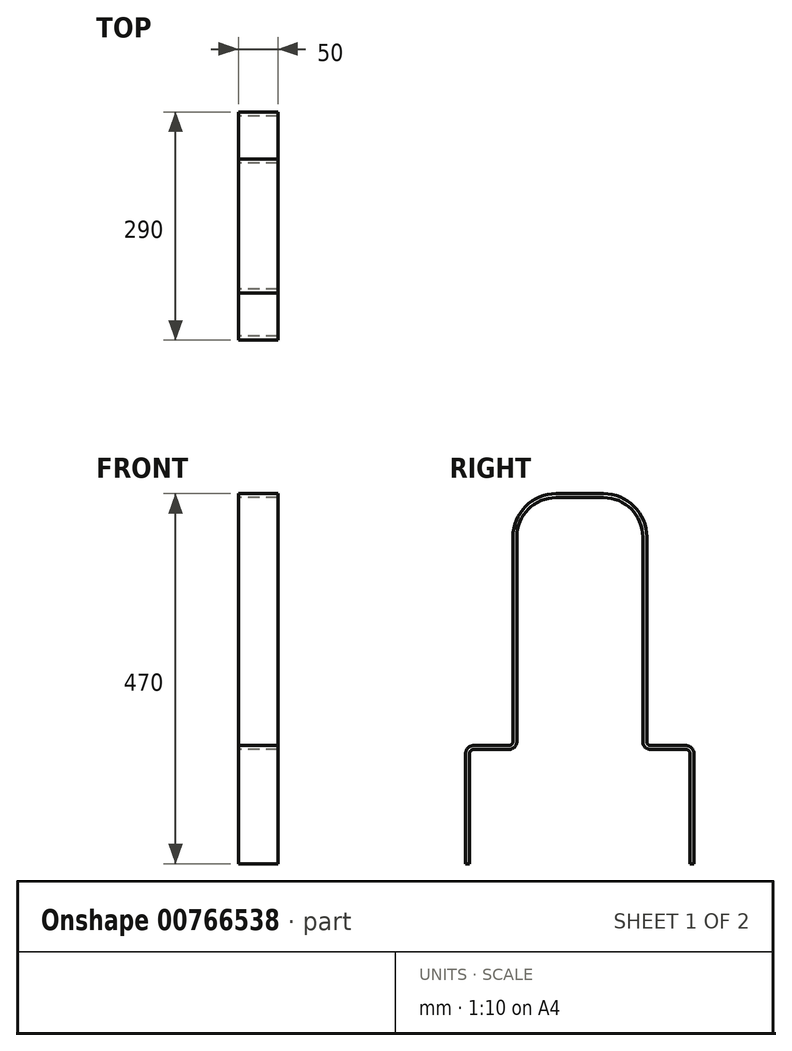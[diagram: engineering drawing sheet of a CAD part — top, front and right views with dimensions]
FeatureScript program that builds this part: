
annotation { "Feature Type Name" : "Feature", "Feature Type Description" : "" }
export const myFeature = defineFeature(function(context is Context, id is Id, definition is map)
    precondition{}
    {
        {
            var Q0;
            Q0=qCreatedBy(makeId("Right.planeOp"),FACE);
            var sketch = newSketch(context, id + "F0", { "sketchPlane" : qUnion([Q0])});
            skLineSegment(sketch, "E0", {"start": v(-145, 0) * mm, "end": v(-145, 140) * mm});
            skLineSegment(sketch, "E1", {"start": v(-135, 150) * mm, "end": v(-90, 150) * mm});
            skLineSegment(sketch, "E2", {"start": v(-85, 155) * mm, "end": v(-85, 415) * mm});
            skLineSegment(sketch, "E3", {"start": v(-30, 470) * mm, "end": v(0, 470) * mm});
            skLineSegment(sketch, "E4", {"start": v(-140, 0) * mm, "end": v(-140, 140) * mm});
            skLineSegment(sketch, "E5", {"start": v(-135, 145) * mm, "end": v(-90, 145) * mm});
            skLineSegment(sketch, "E6", {"start": v(-80, 155) * mm, "end": v(-80, 415) * mm});
            skLineSegment(sketch, "E7", {"start": v(-30, 465) * mm, "end": v(0, 465) * mm});
            skLineSegment(sketch, "E8", {"start": v(-140, 0) * mm, "end": v(-145, 0) * mm});
            skPoint(sketch, "E9.visualSharp", {"position": v(-165, 465) * mm});
            skLineSegment(sketch, "E9.filletArc", {"start": v(-80, 465) * mm, "end": v(-80, 465) * mm});
            skPoint(sketch, "E10.visualSharp", {"position": v(-85, 470) * mm});
            skArc(sketch, "E10.filletArc", {"start": v(-30, 470) * mm, "mid": v(-68.9, 453.9) * mm, "end": v(-85, 415) * mm});
            skPoint(sketch, "E11.visualSharp", {"position": v(-80, 145) * mm});
            skArc(sketch, "E11.filletArc", {"start": v(-90, 145) * mm, "mid": v(-82.93, 147.93) * mm, "end": v(-80, 155) * mm});
            skPoint(sketch, "E12.visualSharp", {"position": v(-85, 150) * mm});
            skArc(sketch, "E12.filletArc", {"start": v(-90, 150) * mm, "mid": v(-86.46, 151.46) * mm, "end": v(-85, 155) * mm});
            skPoint(sketch, "E13.visualSharp", {"position": v(-140, 145) * mm});
            skArc(sketch, "E13.filletArc", {"start": v(-135, 145) * mm, "mid": v(-138.54, 143.54) * mm, "end": v(-140, 140) * mm});
            skPoint(sketch, "E14.visualSharp", {"position": v(-145, 150) * mm});
            skArc(sketch, "E14.filletArc", {"start": v(-135, 150) * mm, "mid": v(-142.07, 147.07) * mm, "end": v(-145, 140) * mm});
            skArc(sketch, "E15.filletArc", {"start": v(-30, 465) * mm, "mid": v(-65.36, 450.36) * mm, "end": v(-80, 415) * mm});
            skPoint(sketch, "E16.MirrorP", {"position": v(165, 465) * mm});
            skArc(sketch, "E17.MirrorCS", {"start": v(30, 465) * mm, "mid": v(65.36, 450.36) * mm, "end": v(80, 415) * mm});
            skLineSegment(sketch, "E18.MirrorCS", {"start": v(140, 0) * mm, "end": v(145, 0) * mm});
            skArc(sketch, "E19.MirrorCS", {"start": v(135, 145) * mm, "mid": v(138.54, 143.54) * mm, "end": v(140, 140) * mm});
            skArc(sketch, "E20.MirrorCS", {"start": v(90, 150) * mm, "mid": v(86.46, 151.46) * mm, "end": v(85, 155) * mm});
            skPoint(sketch, "E21.MirrorP", {"position": v(80, 465) * mm});
            skArc(sketch, "E22.MirrorCS", {"start": v(90, 145) * mm, "mid": v(82.93, 147.93) * mm, "end": v(80, 155) * mm});
            skArc(sketch, "E23.MirrorCS", {"start": v(30, 470) * mm, "mid": v(68.9, 453.9) * mm, "end": v(85, 415) * mm});
            skLineSegment(sketch, "E24.MirrorCS", {"start": v(135, 150) * mm, "end": v(90, 150) * mm});
            skPoint(sketch, "E25.MirrorP", {"position": v(85, 150) * mm});
            skLineSegment(sketch, "E26.MirrorCS", {"start": v(145, 0) * mm, "end": v(145, 140) * mm});
            skPoint(sketch, "E27.MirrorP", {"position": v(140, 145) * mm});
            skLineSegment(sketch, "E28.MirrorCS", {"start": v(30, 470) * mm, "end": v(0, 470) * mm});
            skLineSegment(sketch, "E29.MirrorCS", {"start": v(85, 155) * mm, "end": v(85, 415) * mm});
            skLineSegment(sketch, "E30.MirrorCS", {"start": v(80, 465) * mm, "end": v(80, 465) * mm});
            skLineSegment(sketch, "E31.MirrorCS", {"start": v(80, 155) * mm, "end": v(80, 415) * mm});
            skPoint(sketch, "E32.MirrorP", {"position": v(145, 150) * mm});
            skArc(sketch, "E33.MirrorCS", {"start": v(135, 150) * mm, "mid": v(142.07, 147.07) * mm, "end": v(145, 140) * mm});
            skPoint(sketch, "E34.MirrorP", {"position": v(80, 145) * mm});
            skLineSegment(sketch, "E35.MirrorCS", {"start": v(30, 465) * mm, "end": v(0, 465) * mm});
            skPoint(sketch, "E36.MirrorP", {"position": v(85, 470) * mm});
            skLineSegment(sketch, "E37.MirrorCS", {"start": v(135, 145) * mm, "end": v(90, 145) * mm});
            skLineSegment(sketch, "E38.MirrorCS", {"start": v(140, 0) * mm, "end": v(140, 140) * mm});
            skSolve(sketch);
        }
        {
            var Q0;
            Q0 = qSketchRegion(id + "F0", true);
            extrude(context, id + "F1", {"entities" : qUnion([Q0]), "depth" : 50 * mm, "offsetDistance" : 25 * mm});
        }
    });
